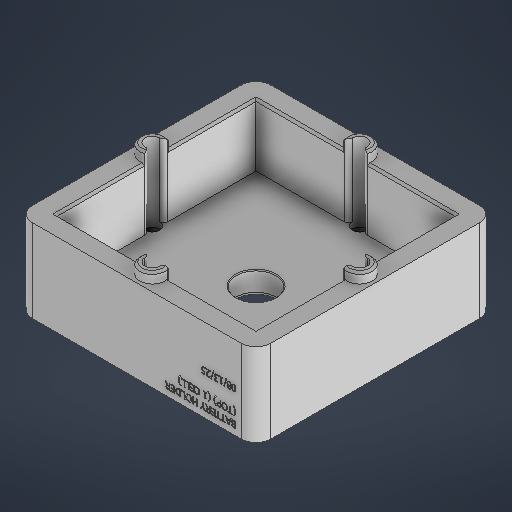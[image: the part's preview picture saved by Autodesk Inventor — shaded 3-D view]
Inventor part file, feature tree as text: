
AUTODESK INVENTOR PART (.ipt)
format: ipt  version: 2025 (Build 290162000, 162)  size: 898,048 bytes
history: native  units: in
note: dims shown in document units (in); Inventor stores cm internally (conversion verified against a paired STEP export)
features: sketch x6, extrude x4, hole x2, fillet x2, chamfer x2
ambient origin geometry x8: Origin, YZ Plane, XZ Plane, XY Plane, X Axis, Y Axis, Z Axis, Center Point
bodies: Solid1 (feature_tree)
feature tree (16):
  extrude  "Extrusion1"  Depth=4.5276in
  sketch  "Sketch4"  dims[d2=0.3937in d3=0.0in d48=3.7795in]
  extrude  "Extrusion3"  Depth=3.7795in
  hole  "Hole4"  [1 undecoded]
  hole  "Hole5"  [1 undecoded]
  extrude  "Extrusion4"  Depth=0.2362in
  fillet  "Fillet1"  Radius=0.4724in
  fillet  "Fillet2"  Radius=0.4724in
  chamfer  "Chamfer1"  Distance=0.4724in
  chamfer  "Chamfer2"  Distance=0.4724in
  extrude  "Extrusion5"  Depth=0.1969in TaperAngle=0.0deg
  sketch  "Sketch1"  dims[d0=4.5276in d1=4.5276in]
  sketch  "Sketch6"  dims[d49=3.7795in d174=1.1811in d175=0.0in]
  sketch  "Sketch Rectangular Pattern14"  dims[d186=1.1811in d188=1.9685in d189=1.1811in d191=1.9685in d194=0.2805in d195=0.2362in d196=0.5118in d197=0.2756in d198=0.0172in d199=0.315in d200=0.8108in d201=0.4724in d202=0.4724in d203=0.4724in d204=0.4724in d205=0.1969in d206=0.0in d207=0.2805in d208=0.0787in d209=0.0157in d210=0.0787in d211=45.0deg d212=0.0394in d213=0.0787in d214=45.0deg d215=0.0787in d216=0.0in d217=0.748in]
  sketch  "Sketch7"  dims[d176=0.7323in d177=0.2362in d178=0.748in d179=0.0787in d180=0.0172in d181=0.315in d182=0.8108in d183=3.937in]
  sketch  "Sketch8"  dims[d184=3.937in d185=0.2362in]
note: 2 required parameter values undecoded (feature->parameter linkage not recoverable at this tier; creation-order binding heuristic only, values carry confidence <= 0.55)
